# Revit family: Haworth_Kennedee_Sectional_Corner90
name_source: partatom
category: Furniture
revit_build: Autodesk Revit 2018 (Build: 20170223_1515(x64)
units: mm (PartAtom-declared; Revit-internal decimal feet)

## family parameters
Always vertical = Yes
Cut with Voids When Loaded = No
OmniClass Number = 23.40.70.14.64.21
OmniClass Title = Systems Furniture
Room Calculation Point = No
Shared = No
Work Plane-Based = No

## types (2) — shared parameters
Assembly Code = E2020200
Back Depth = 11"
Back Length = 36"
Base Finish = Haworth _ Paint _ Metallic Gunmetal
Bench Width = 36 1/4"
Leg Offset = 16 1/2"
Leg Thickness Half = 1"
Manufacturer = Haworth
Model = HCPF-KEB
Revision Number = 4
Size = Verify Final Dim. w/ Haworth
URL = http://www.haworth.com
URL - Product = http://www.haworth.com
Warranty = http://www.haworth.com

## per-type parameters (varying)
| type | Description | No Back Cushion | Seat Width | With Back Cushion |
| HCPF-KEB - With Back Cushion | Haworth Kennedee Sectional Corner 90 - With Back Cushion | No | 25 1/4" | Yes |
| HCPF-KEB - No Back Cushion | Haworth Kennedee Sectional Corner 90 - No Back Cushion | Yes | 36 1/4" | No |

## geometry (parser evidence)
native form markers: Sweep x7
no freeform markers — native parametric forms only
